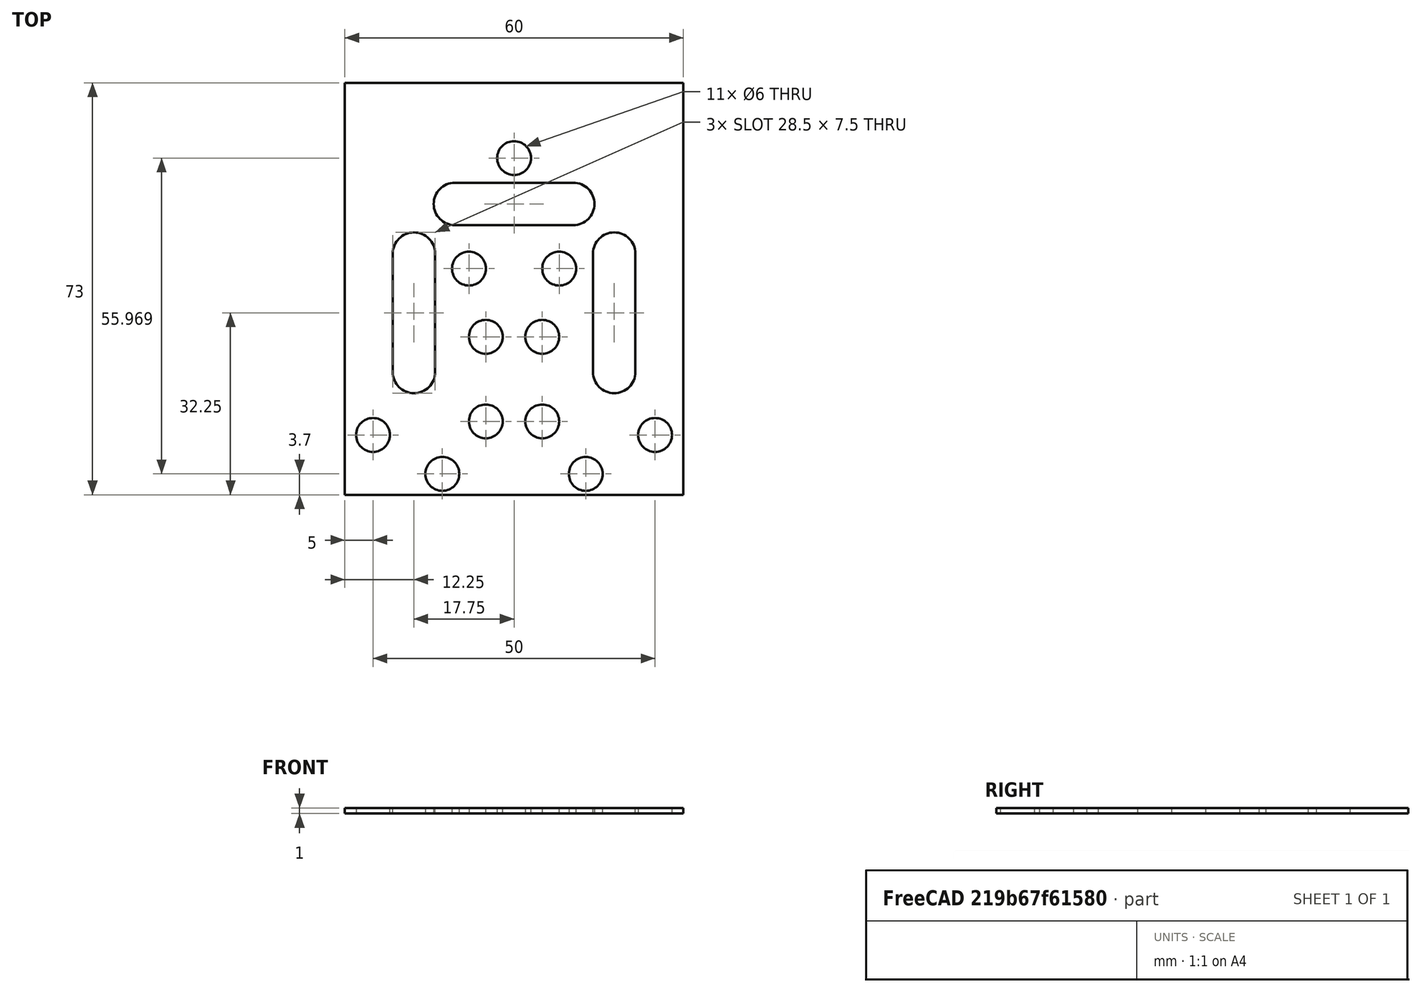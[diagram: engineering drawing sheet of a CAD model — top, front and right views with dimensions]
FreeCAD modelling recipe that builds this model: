
FCSTD DOCUMENT  (FreeCAD 0.18.4R)
Label: main_head_PnP_v1.01
License: All rights reserved
LicenseURL: http://en.wikipedia.org/wiki/All_rights_reserved
objects: Sketcher::SketchObject×1, PartDesign::Pad×1, PartDesign::Body×1
note: 4 computed .brp shape members not serialized (recipe doc carries the construction recipe); baked Part::Feature solids carry a one-line shape summary decoded from their .brp

FEATURE [Sketcher::SketchObject] Sketch
  MapMode = 5
  Support = -> [XY_Plane]
  sketch-geometry (31):
    g0: LineSegment StartX=30 StartY=-63 StartZ=0 EndX=-30 EndY=-63 EndZ=0
    g1: LineSegment StartX=-30 StartY=-63 StartZ=0 EndX=-30 EndY=10 EndZ=0
    g2: LineSegment StartX=-30 StartY=10 StartZ=0 EndX=0 EndY=10 EndZ=0
    g3: LineSegment StartX=30 StartY=-2 StartZ=0 EndX=30 EndY=-22 EndZ=0
    g4: LineSegment StartX=30 StartY=-41 StartZ=0 EndX=30 EndY=-63 EndZ=0
    g5: Circle CenterX=-12.71 CenterY=-59.3 CenterZ=0 NormalX=0 NormalY=0 NormalZ=1 AngleXU=0 Radius=3
    g6: Circle CenterX=12.71 CenterY=-59.3 CenterZ=0 NormalX=0 NormalY=0 NormalZ=1 AngleXU=0 Radius=3
    g7: ArcOfCircle CenterX=-17.75 CenterY=-41.25 CenterZ=0 NormalX=0 NormalY=0 NormalZ=1 AngleXU=0 Radius=3.85 StartAngle=3.14159 EndAngle=6.28319
    g8: ArcOfCircle CenterX=-17.75 CenterY=-20.25 CenterZ=0 NormalX=0 NormalY=0 NormalZ=1 AngleXU=0 Radius=3.85 StartAngle=0 EndAngle=3.14159
    g9: LineSegment StartX=-13.9 StartY=-41.25 StartZ=0 EndX=-13.9 EndY=-20.25 EndZ=0
    g10: LineSegment StartX=-21.6 StartY=-41.25 StartZ=0 EndX=-21.6 EndY=-20.25 EndZ=0
    g11: ArcOfCircle CenterX=17.75 CenterY=-41.25 CenterZ=0 NormalX=0 NormalY=0 NormalZ=1 AngleXU=0 Radius=3.85 StartAngle=3.14159 EndAngle=6.28319
    g12: ArcOfCircle CenterX=17.75 CenterY=-20.25 CenterZ=0 NormalX=0 NormalY=0 NormalZ=1 AngleXU=0 Radius=3.85 StartAngle=0 EndAngle=3.14159
    g13: LineSegment StartX=21.6 StartY=-41.25 StartZ=0 EndX=21.6 EndY=-20.25 EndZ=0
    g14: LineSegment StartX=13.9 StartY=-41.25 StartZ=0 EndX=13.9 EndY=-20.25 EndZ=0
    g15: ArcOfCircle CenterX=-10.5 CenterY=-11.45 CenterZ=0 NormalX=0 NormalY=0 NormalZ=1 AngleXU=0 Radius=3.85 StartAngle=1.5708 EndAngle=4.71239
    g16: ArcOfCircle CenterX=10.5 CenterY=-11.45 CenterZ=0 NormalX=0 NormalY=0 NormalZ=1 AngleXU=0 Radius=3.85 StartAngle=4.71239 EndAngle=7.85398
    g17: LineSegment StartX=-10.5 StartY=-15.3 StartZ=0 EndX=10.5 EndY=-15.3 EndZ=0
    g18: LineSegment StartX=-10.5 StartY=-7.6 StartZ=0 EndX=10.5 EndY=-7.6 EndZ=0
    g19: Circle CenterX=0 CenterY=-3.33121 CenterZ=0 NormalX=0 NormalY=0 NormalZ=1 AngleXU=0 Radius=3
    g20: Circle CenterX=-8 CenterY=-22.9179 CenterZ=0 NormalX=0 NormalY=0 NormalZ=1 AngleXU=0 Radius=3
    g21: Circle CenterX=8 CenterY=-22.9179 CenterZ=0 NormalX=0 NormalY=0 NormalZ=1 AngleXU=0 Radius=3
    g22: Circle CenterX=-5 CenterY=-35 CenterZ=0 NormalX=0 NormalY=0 NormalZ=1 AngleXU=0 Radius=3
    g23: Circle CenterX=5 CenterY=-35 CenterZ=0 NormalX=0 NormalY=0 NormalZ=1 AngleXU=0 Radius=3
    g24: Circle CenterX=-5 CenterY=-50 CenterZ=0 NormalX=0 NormalY=0 NormalZ=1 AngleXU=0 Radius=3
    g25: Circle CenterX=5 CenterY=-50 CenterZ=0 NormalX=0 NormalY=0 NormalZ=1 AngleXU=0 Radius=3
    g26: LineSegment StartX=30 StartY=-41 StartZ=0 EndX=30 EndY=-22 EndZ=0
    g27: LineSegment StartX=0 StartY=10 StartZ=0 EndX=30 EndY=10 EndZ=0
    g28: LineSegment StartX=30 StartY=-2 StartZ=0 EndX=30 EndY=10 EndZ=0
    g29: Circle CenterX=-25 CenterY=-52.3926 CenterZ=0 NormalX=0 NormalY=0 NormalZ=1 AngleXU=0 Radius=3
    g30: Circle CenterX=25 CenterY=-52.3926 CenterZ=0 NormalX=0 NormalY=0 NormalZ=1 AngleXU=0 Radius=3
  constraints (74):
    c: Vertical(g1)
    c: DistanceY(g1,g1) = 73
    c: Distance(g0,g0) = 60
    c: Coincident(g2,g1)
    c: PointOnObject(g2,g-2)
    c: Horizontal(g2)
    c: Vertical(g3)
    c: Coincident(g4,g0)
    c: Vertical(g4)
    c: DistanceY(g-1,g1) = 10
    c: Coincident(g0,g1)
    c: Symmetric(g0,g0,g-2)
    c: Symmetric(g5,g6,g-2)
    c: Distance(g6,g5) = 25.42
    c: Radius(g5) = 3
    c: Radius(g6) = 3
    c: Tangent(g7,g10) = 1.5708
    c: Tangent(g7,g9) = -1.5708
    c: Tangent(g9,g8) = -1.5708
    c: Tangent(g10,g8) = 1.5708
    c: Vertical(g9)
    c: Equal(g7,g8)
    c: Tangent(g11,g14) = 1.5708
    c: Tangent(g11,g13) = -1.5708
    c: Tangent(g13,g12) = -1.5708
    c: Tangent(g14,g12) = 1.5708
    c: Vertical(g13)
    c: Equal(g11,g12)
    c: Tangent(g15,g18) = 1.5708
    c: Tangent(g15,g17) = -1.5708
    c: Tangent(g17,g16) = -1.5708
    c: Tangent(g18,g16) = 1.5708
    c: Horizontal(g17)
    c: Distance(g8,g7) = 21
    c: Distance(g12,g11) = 21
    c: Distance(g15,g16) = 21
    c: Distance(g8,g8) = 7.7
    c: Distance(g15,g15) = 7.7
    c: Distance(g12,g12) = 7.7
    c: Symmetric(g15,g16,g-2)
    c: Symmetric(g8,g12,g-2)
    c: PointOnObject(g19,g-2)
    c: Radius(g19) = 3
    c: Symmetric(g20,g21,g-2)
    c: Radius(g20) = 3
    c: Radius(g21) = 3
    c: Distance(g20,g21) = 16
    c: Horizontal(g24,g25)
    c: Vertical(g22,g24)
    c: Vertical(g23,g25)
    c: Symmetric(g22,g23,g-2)
    c: Distance(g22,g23) = 10
    c: Distance(g24,g22) = 15
    c: Radius(g22) = 3
    c: Radius(g23) = 3
    c: Radius(g25) = 3
    c: Radius(g24) = 3
    c: Distance(g5,g0) = 3.7
    c: Distance(g24,g0) = 13
    c: Coincident(g26,g4)
    c: Coincident(g26,g3)
    c: Vertical(g4,g3)
    c: Coincident(g27,g2)
    c: Horizontal(g27)
    c: Coincident(g28,g3)
    c: Coincident(g28,g27)
    c: Vertical(g28)
    c: Distance(g7,g0) = 21.75
    c: Symmetric(g30,g29,g-2)
    c: Distance(g29,g30) = 50
    c: Radius(g29) = 3
    c: Radius(g30) = 3
    c: Distance(g11,g7) = 35.5
    c: Distance(g15,g2) = 21.45
FEATURE [PartDesign::Pad] Pad
  Length = 1
  Length2 = 100
  Profile = -> Sketch
  Type = 0
FEATURE [PartDesign::Body] Body
  Group = -> [Sketch,Pad]
  Origin = -> Origin
  Tip = -> Pad
